# Revit family: TD92_SOF272_VER040_RVT20_R00
name_source: partatom
category: Mobiliário
units: mm (PartAtom-declared; Revit-internal decimal feet)

## family parameters
Com base no plano de trabalho = Não
Compartilhado = Não
Corte com vazios quando carregada = Não
Número OmniClass = 23.40.20.00
Ponto de cálculo do ambiente = Não
Sempre na vertical = Sim
Título OmniClass = General Furniture and Specialties

## types (1)
- TD92_SOF272_VER040_RVT20_R00
    Descrição = Nada melhor que saber que nossas crianças estão desenvolvendo suas atividades com equipamentos seguros e de qualidade, não é mesmo?! E a Cadeira Tramontina Sofia Infantil em Polipropileno e Fibra de Vidro é uma excelente opção para quem se preocupa com isso. O produto possui altura adequada para o conforto e segurança das crianças, além de ter o assento e encosto pensados para se adequar à anatomia infantil. Ela é produzida em polipropileno e fibra de vidro, materiais que proporcionam maior resistência e durabilidade. Possui design e cor especiais que irão chamar a atenção dos pequenos e que vão garantir a diversão que eles tanto merecem!
    Elevação padrão = 0  [stored 0 ft]
    Fabricante = Tramontina Delta S/A
    Modelo = Cadeira Infantil Tramontina Sofia em Polipropileno e Fibra de Vidro Vermelho
    Nota-chave = 92272040

note: [stored X ft] marks values corroborated as IEEE doubles in the binary element streams (Revit-internal decimal feet)
